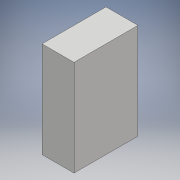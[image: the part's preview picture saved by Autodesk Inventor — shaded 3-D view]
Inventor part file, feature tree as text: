
AUTODESK INVENTOR PART (.ipt)
format: ipt  version: 2017 (Build 210142000, 142)  size: 227,328 bytes
history: native  units: mm
features: extrude x3, sketch x3, other x1
ambient origin geometry x8: Origin, YZ Plane, XZ Plane, XY Plane, X Axis, Y Axis, Z Axis, Center Point
bodies: Body1 (feature_tree)
feature tree (7):
  other  "Твердое тело1"
  extrude  "Выдавливание1"  Depth=10.0mm
  sketch  "Эскиз2"
  extrude  "Выдавливание2"  Depth=30.0mm
  extrude  "Выдавливание3"  Depth=20.0mm TaperAngle=0.0deg
  sketch  "Эскиз1"
  sketch  "Эскиз3"
